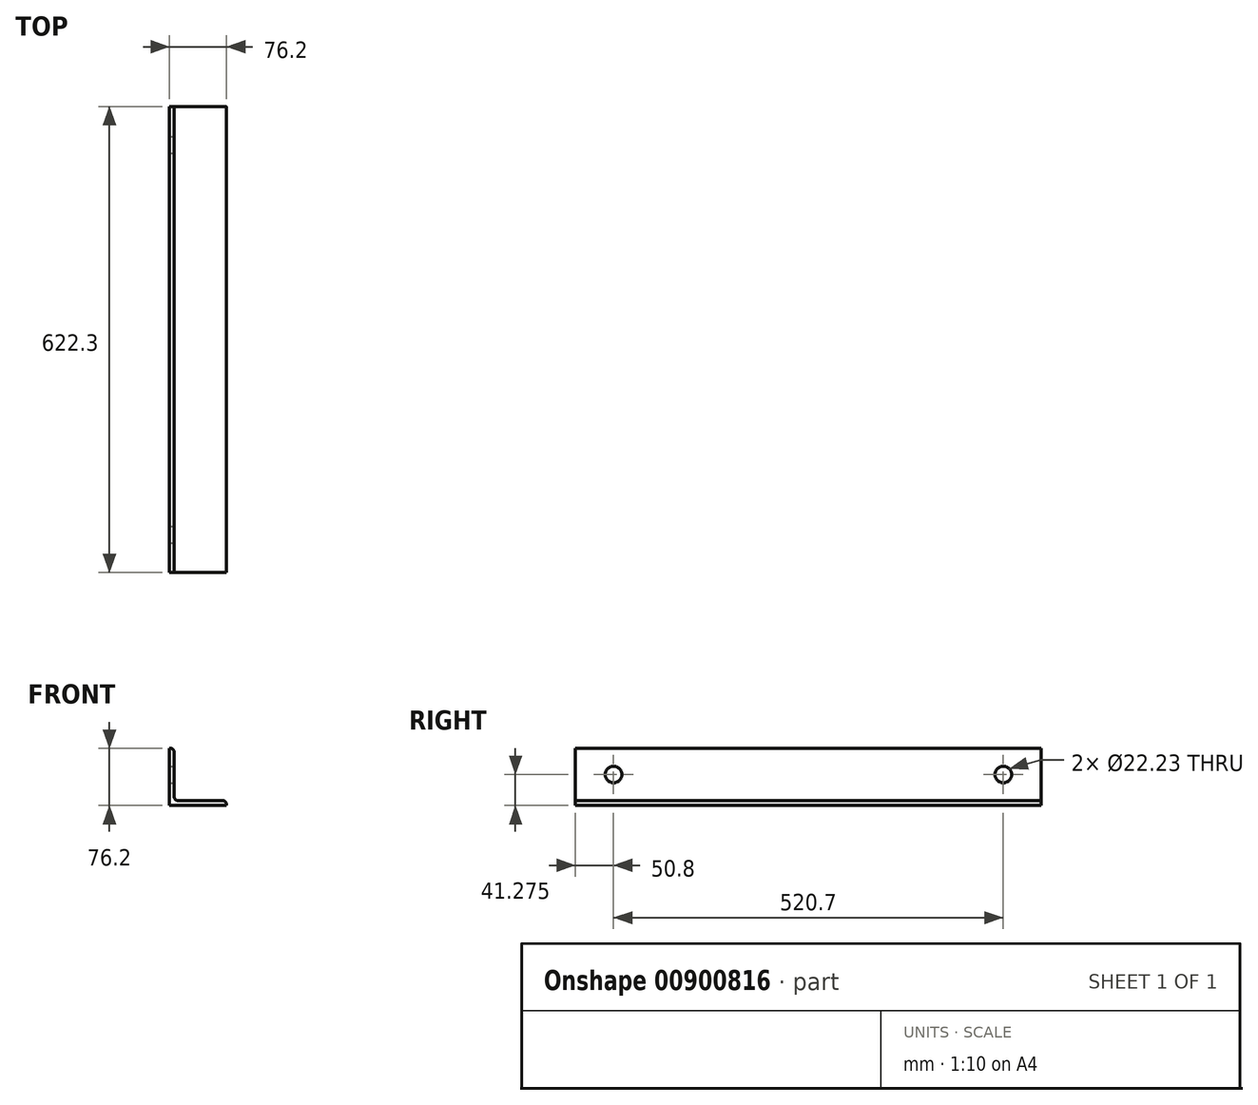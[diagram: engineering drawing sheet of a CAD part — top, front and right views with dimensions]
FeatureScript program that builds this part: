
annotation { "Feature Type Name" : "Feature", "Feature Type Description" : "" }
export const myFeature = defineFeature(function(context is Context, id is Id, definition is map)
    precondition{}
    {
        {
            var Q0;
            Q0=qCreatedBy(makeId("Front.planeOp"),FACE);
            var sketch = newSketch(context, id + "F0", { "sketchPlane" : qUnion([Q0])});
            skLineSegment(sketch, "E0.bottom", {"start": v(38.1, -38.1) * mm, "end": v(-38.1, -38.1) * mm});
            skLineSegment(sketch, "E0.top", {"start": v(-31.75, 38.1) * mm, "end": v(-38.1, 38.1) * mm});
            skLineSegment(sketch, "E0.left", {"start": v(38.1, -38.1) * mm, "end": v(38.1, -31.75) * mm});
            skLineSegment(sketch, "E0.right", {"start": v(-38.1, -38.1) * mm, "end": v(-38.1, 38.1) * mm});
            skPoint(sketch, "E0.middle", {"position": v(0, 0) * mm});
            skLineSegment(sketch, "E1.0", {"start": v(-31.75, -31.75) * mm, "end": v(-31.75, 38.1) * mm});
            skLineSegment(sketch, "E2.0", {"start": v(38.1, -31.75) * mm, "end": v(-31.75, -31.75) * mm});
            skPoint(sketch, "E3.orphan", {"position": v(38.1, 38.1) * mm});
            skSolve(sketch);
        }
        {
            var Q0;
            Q0 = qSketchRegion(id + "F0", true);
            extrude(context, id + "F1", {"entities" : qUnion([Q0]), "depth" : 622.3 * mm, "offsetDistance" : 25.4 * mm, "symmetric" : true});
        }
        {
            var Q0;
            Q0=makeQuery(id+"F1.opExtrude","SWEPT_EDGE",EDGE,{"disambiguationData":[OSD([sQuery(id+"F0.wireOp",EDGE,"E0.top"),sQuery(id+"F0.wireOp",EDGE,"E1.0")])]});
            var Q1;
            Q1=makeQuery(id+"F1.opExtrude","SWEPT_EDGE",EDGE,{"disambiguationData":[OSD([sQuery(id+"F0.wireOp",EDGE,"E1.0"),sQuery(id+"F0.wireOp",EDGE,"E2.0")])]});
            var Q2;
            Q2=makeQuery(id+"F1.opExtrude","SWEPT_EDGE",EDGE,{"disambiguationData":[OSD([sQuery(id+"F0.wireOp",EDGE,"E0.left"),sQuery(id+"F0.wireOp",EDGE,"E2.0")])]});
            fillet(context, id + "F2", {"entities" : qUnion([Q0, Q1, Q2]), "radius" : 5.08 * mm, "tangentPropagation" : true, "allowEdgeOverflow" : false});
        }
        {
            var Q0;
            Q0=makeQuery(id+"F1.opExtrude","SWEPT_FACE",FACE,{"disambiguationData":[OSD([sQuery(id+"F0.wireOp",EDGE,"E1.0")])]});
            var sketch = newSketch(context, id + "F3", { "sketchPlane" : qUnion([Q0])});
            skCircle(sketch, "E4", {"center": v(260.35, 3.17) * mm, "radius": 11.11 * mm});
            skPoint(sketch, "E4.centerSnap0", {"position": v(311.15, 3.17) * mm});
            skCircle(sketch, "E5.MirrorC", {"center": v(-260.35, 3.17) * mm, "radius": 11.11 * mm});
            skSolve(sketch);
        }
        {
            var Q0;
            Q0 = qSketchRegion(id + "F3", true);
            extrude(context, id + "F4", {"entities" : qUnion([Q0]), "operationType" : NewBodyOperationType.REMOVE, "oppositeDirection" : true, "depth" : 25.4 * mm, "offsetDistance" : 25.4 * mm});
        }
    });
